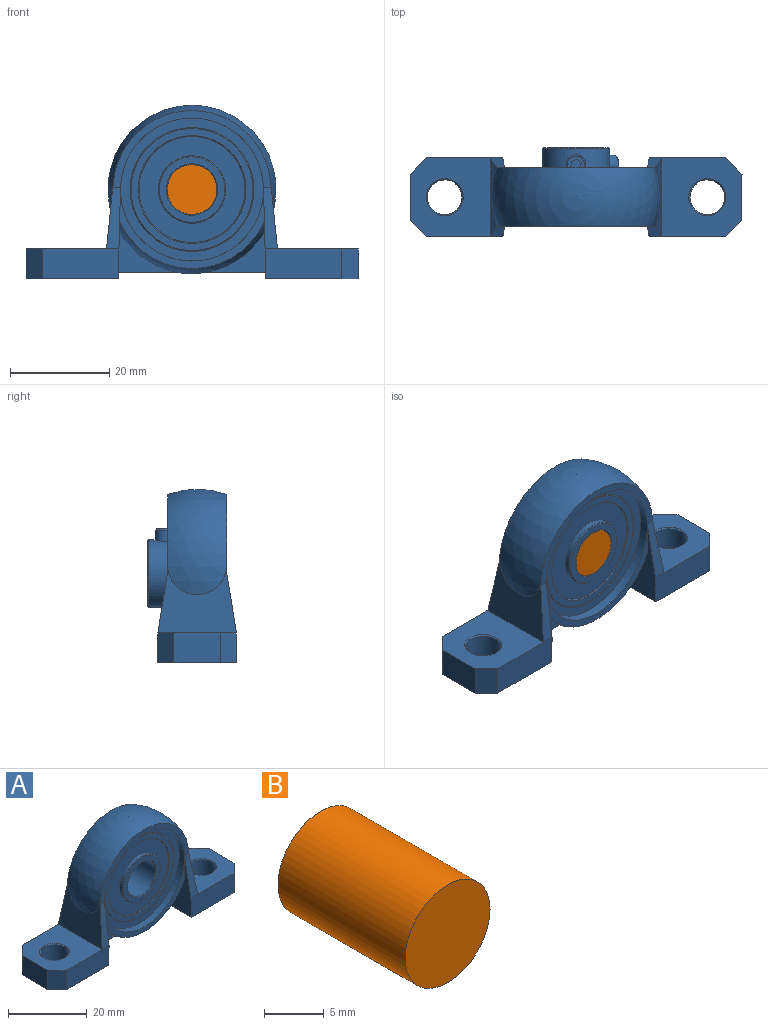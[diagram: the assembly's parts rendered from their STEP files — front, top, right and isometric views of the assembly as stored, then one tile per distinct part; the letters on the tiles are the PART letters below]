
ASSEMBLY  parts=2 mates=1
PART A: 89 faces, bbox 67.9x34.9x35.9 mm
  f0: plane 11.94x2.5mm, normal (0,0,-1), area 29.4mm2, adj f1,f2,f87,f88
  f1: plane 11.94x8.18mm, normal (0,-1,0), area 33.6mm2, adj f0,f2,f88
  f2: plane 19.23x16.71mm, normal (-1,0,-0.03), area 148.1mm2, adj f0,f1,f3,f81,f82,f83,f84,f85
  f3: plane 29.2x16.3mm, normal (0,-1,0), area 59.1mm2, adj f2,f4,f80,f88
  f4: plane 19.23x16.71mm, normal (1,0,-0.03), area 148.1mm2, adj f3,f5,f6,f7,f75,f76,f77,f78
  f5: plane 11.94x2.5mm, normal (0,0,-1), area 29.4mm2, adj f4,f6,f79,f88
  f6: plane 11.94x8.18mm, normal (0,1,0), area 33.6mm2, adj f4,f5,f88
  f7: plane 12.37x2.82mm, normal (0,0.99,0.16), area 25.4mm2, adj f4,f8,f68,f75
  f8: plane 31.96x15.56mm, normal (0,1,0), area 70.5mm2, adj f7,f9,f17,f18,f68,f85
  f9: plane 15.85x13.62mm, normal (0.99,0,0.1), area 132mm2, adj f8,f10,f16,f17,f81,f85
  f10: plane 16.25x15.85mm, normal (0,0,1), area 202.9mm2, adj f9,f11,f13,f14,f15,f82,f84
  f11: cone r=3.75mm half-angle=45deg, axis (0,0,1), area 8.1mm2, adj f10,f12
  f12: cylinder r=3.5mm len=7mm, axis (0,0,1), area 126.4mm2, adj f11,f83
  f13: plane 6x3.25mm, normal (0.71,0.71,0), area 27.6mm2, adj f10,f14,f83,f84
  f14: plane 9.35x6mm, normal (1,0,0), area 56.1mm2, adj f10,f13,f15,f83
  f15: plane 6x3.25mm, normal (0.71,-0.71,0), area 27.6mm2, adj f10,f14,f82,f83
  f16: plane 31.96x15.56mm, normal (0,-1,0), area 70.5mm2, adj f9,f17,f68,f78,f80,f81
  f17: sphere r=17mm, area 705.6mm2, adj f8,f9,f16,f68
  f18: cylinder r=14.43mm len=28.87mm, axis (0,1,0), area 174.6mm2, adj f8,f19,f86
  f19: plane 28.87x28.87mm, normal (0,1,0), area 163.7mm2, adj f18,f20
  f20: cylinder r=12.5mm len=25mm, axis (0,1,0), area 15.7mm2, adj f19,f21
  f21: cone r=12.3mm half-angle=45deg, axis (0,-1,0), area 22mm2, adj f20,f22
  f22: plane 24.6x24.6mm, normal (0,1,0), area 102mm2, adj f21,f23
  f23: cone r=10.9mm half-angle=45deg, axis (0,1,0), area 19.2mm2, adj f22,f24
  f24: cylinder r=10.7mm len=21.4mm, axis (0,1,0), area 3.4mm2, adj f23,f25
  f25: plane 21.4x21.4mm, normal (0,1,0), area 214.4mm2, adj f24,f26
  f26: cylinder r=6.8mm len=13.6mm, axis (0,1,0), area 232.7mm2, adj f25,f27,f37,f47
  f27: cylinder r=2mm len=4mm, axis (0,0,1), area 28.3mm2, adj f26,f28
  f28: cone r=1.75mm half-angle=45deg, axis (0,0,-1), area 4.2mm2, adj f27,f29
  f29: plane 3.5x3.5mm, normal (0,0,1), area 6.2mm2, adj f28,f30,f32,f33,f34,f35,f36
  f30: plane 2x1.15mm, normal (-1,0.06,0), area 2.3mm2, adj f29,f31,f32,f36
  f31: plane 2.3x2.07mm, normal (0,0,1), area 3.5mm2, adj f30,f32,f33,f34,f35,f36
  f32: plane 2x0.96mm, normal (-0.55,-0.83,0), area 2.3mm2, adj f29,f30,f31,f33
  f33: plane 2x1.03mm, normal (0.45,-0.89,0), area 2.3mm2, adj f29,f31,f32,f34
  f34: plane 2x1.15mm, normal (1,-0.06,0), area 2.3mm2, adj f29,f31,f33,f35
  f35: plane 2x0.96mm, normal (0.55,0.83,0), area 2.3mm2, adj f29,f31,f34,f36
  f36: plane 2x1.03mm, normal (-0.45,0.89,0), area 2.3mm2, adj f29,f30,f31,f35
  f37: cylinder r=2mm len=4.59mm, axis (0.87,0,-0.5), area 28.3mm2, adj f26,f38
  f38: cone r=1.75mm half-angle=45deg, axis (-0.87,0,0.5), area 4.2mm2, adj f37,f39
  f39: plane 3.5x3.03mm, normal (0.87,0,-0.5), area 6.2mm2, adj f38,f40,f42,f43,f44,f45,f46
  f40: plane 1.77x1.15mm, normal (0.5,0.06,0.86), area 2.3mm2, adj f39,f41,f42,f46
  f41: plane 2.3x1.79mm, normal (0.87,0,-0.5), area 3.5mm2, adj f40,f42,f43,f44,f45,f46
  f42: plane 2.21x1.83mm, normal (0.28,-0.83,0.48), area 2.3mm2, adj f39,f40,f41,f43
  f43: plane 2.25x1.89mm, normal (-0.22,-0.89,-0.39), area 2.3mm2, adj f39,f41,f42,f44
  f44: plane 1.77x1.15mm, normal (-0.5,-0.06,-0.86), area 2.3mm2, adj f39,f41,f43,f45
  f45: plane 2.21x1.83mm, normal (-0.28,0.83,-0.48), area 2.3mm2, adj f39,f41,f44,f46
  f46: plane 2.25x1.89mm, normal (0.22,0.89,0.39), area 2.3mm2, adj f39,f40,f41,f45
  f47: cone r=6.6mm half-angle=45deg, axis (0,-1,0), area 11.9mm2, adj f26,f48
  f48: plane 13.2x13.2mm, normal (0,1,0), area 51.9mm2, adj f47,f49
  f49: cone r=5.2mm half-angle=45deg, axis (0,1,0), area 9.1mm2, adj f48,f50
  f50: cylinder r=5mm len=14.6mm, axis (0,1,0), area 439.1mm2, adj f49,f51,f53,f54,f56,f57
  f51: cylinder r=1.75mm len=3.5mm, axis (0,0,1), area 0mm2, adj f50,f52
  f52: plane 3.5x3.5mm, normal (0,0,-1), area 9.6mm2, adj f51,f53
  f53: cylinder r=1.75mm len=3.5mm, axis (0,0,1), area 0mm2, adj f50,f52
  f54: cylinder r=1.75mm len=3.5mm, axis (0.87,0,-0.5), area 0mm2, adj f50,f55
  f55: plane 3.5x3.03mm, normal (-0.87,0,0.5), area 9.6mm2, adj f54,f56
  f56: cylinder r=1.75mm len=3.5mm, axis (0.87,0,-0.5), area 0mm2, adj f50,f55
  f57: cone r=5.2mm half-angle=45deg, axis (0,-1,0), area 9.1mm2, adj f50,f58
  f58: plane 13.2x13.2mm, normal (0,-1,0), area 51.9mm2, adj f57,f59
  f59: cone r=6.6mm half-angle=45deg, axis (0,1,0), area 11.9mm2, adj f58,f60
  f60: cylinder r=6.8mm len=13.6mm, axis (0,1,0), area 44.9mm2, adj f59,f61
  f61: plane 21.4x21.4mm, normal (0,-1,0), area 214.4mm2, adj f60,f62
  f62: cylinder r=10.7mm len=21.4mm, axis (0,1,0), area 3.4mm2, adj f61,f63
  f63: cone r=10.9mm half-angle=45deg, axis (0,-1,0), area 19.2mm2, adj f62,f64
  f64: plane 24.6x24.6mm, normal (0,-1,0), area 102mm2, adj f63,f65
  f65: cone r=12.3mm half-angle=45deg, axis (0,1,0), area 22mm2, adj f64,f66
  f66: cylinder r=12.5mm len=25mm, axis (0,1,0), area 15.7mm2, adj f65,f67
  f67: plane 28.87x28.87mm, normal (0,-1,0), area 163.7mm2, adj f66,f80
  f68: plane 15.85x13.62mm, normal (-0.99,0,0.1), area 132mm2, adj f7,f8,f16,f17,f69,f78
  f69: plane 16.25x15.85mm, normal (0,0,1), area 202.9mm2, adj f68,f70,f72,f73,f74,f75,f77
  f70: cone r=3.75mm half-angle=45deg, axis (0,0,1), area 8.1mm2, adj f69,f71
  f71: cylinder r=3.5mm len=7mm, axis (0,0,1), area 126.4mm2, adj f70,f76
  f72: plane 9.35x6mm, normal (-1,0,0), area 56.1mm2, adj f69,f73,f74,f76
  f73: plane 6x3.25mm, normal (-0.71,0.71,0), area 27.6mm2, adj f69,f72,f75,f76
  f74: plane 6x3.25mm, normal (-0.71,-0.71,0), area 27.6mm2, adj f69,f72,f76,f77
  f75: plane 15.5x6mm, normal (0,1,0), area 92.6mm2, adj f4,f7,f69,f73,f76
  f76: plane 18.6x15.85mm, normal (0,0,-1), area 245.8mm2, adj f4,f71,f72,f73,f74,f75,f77
  f77: plane 15.5x6mm, normal (0,-1,0), area 92.6mm2, adj f4,f69,f74,f76,f78
  f78: plane 12.37x2.82mm, normal (0,-0.99,0.16), area 25.4mm2, adj f4,f16,f68,f77
  f79: plane 11.94x8.18mm, normal (0,-1,0), area 33.6mm2, adj f4,f5,f88
  f80: cylinder r=14.43mm len=28.87mm, axis (0,1,0), area 174.6mm2, adj f3,f16,f67
  f81: plane 12.37x2.82mm, normal (0,-0.99,0.16), area 25.4mm2, adj f2,f9,f16,f82
  f82: plane 15.5x6mm, normal (0,-1,0), area 92.6mm2, adj f2,f10,f15,f81,f83
  f83: plane 18.6x15.85mm, normal (0,0,-1), area 245.8mm2, adj f2,f12,f13,f14,f15,f82,f84
  f84: plane 15.5x6mm, normal (0,1,0), area 92.6mm2, adj f2,f10,f13,f83,f85
  f85: plane 12.37x2.82mm, normal (0,0.99,0.16), area 25.4mm2, adj f2,f8,f9,f84
  f86: plane 29.2x16.3mm, normal (0,1,0), area 59.1mm2, adj f2,f4,f18,f88
  f87: plane 11.94x8.18mm, normal (0,1,0), area 33.6mm2, adj f0,f2,f88
  f88: sphere r=17mm, area 366.6mm2, adj f0,f1,f2,f3,f4,f5,f6,f79
PART B: 3 faces, bbox 10x15x10 mm
  f0: plane 10x10mm, normal (0,1,0), area 78.5mm2, adj f2
  f1: plane 10x10mm, normal (0,-1,0), area 78.5mm2, adj f2
  f2: cylinder r=5mm len=15mm, axis (0,-1,0), area 471.2mm2, adj f0,f1
PLACE A at identity
PLACE B at identity
MATE revolute A.f57 <-> B.f2  axis (0,-1,0) through (0,-5,0)mm
